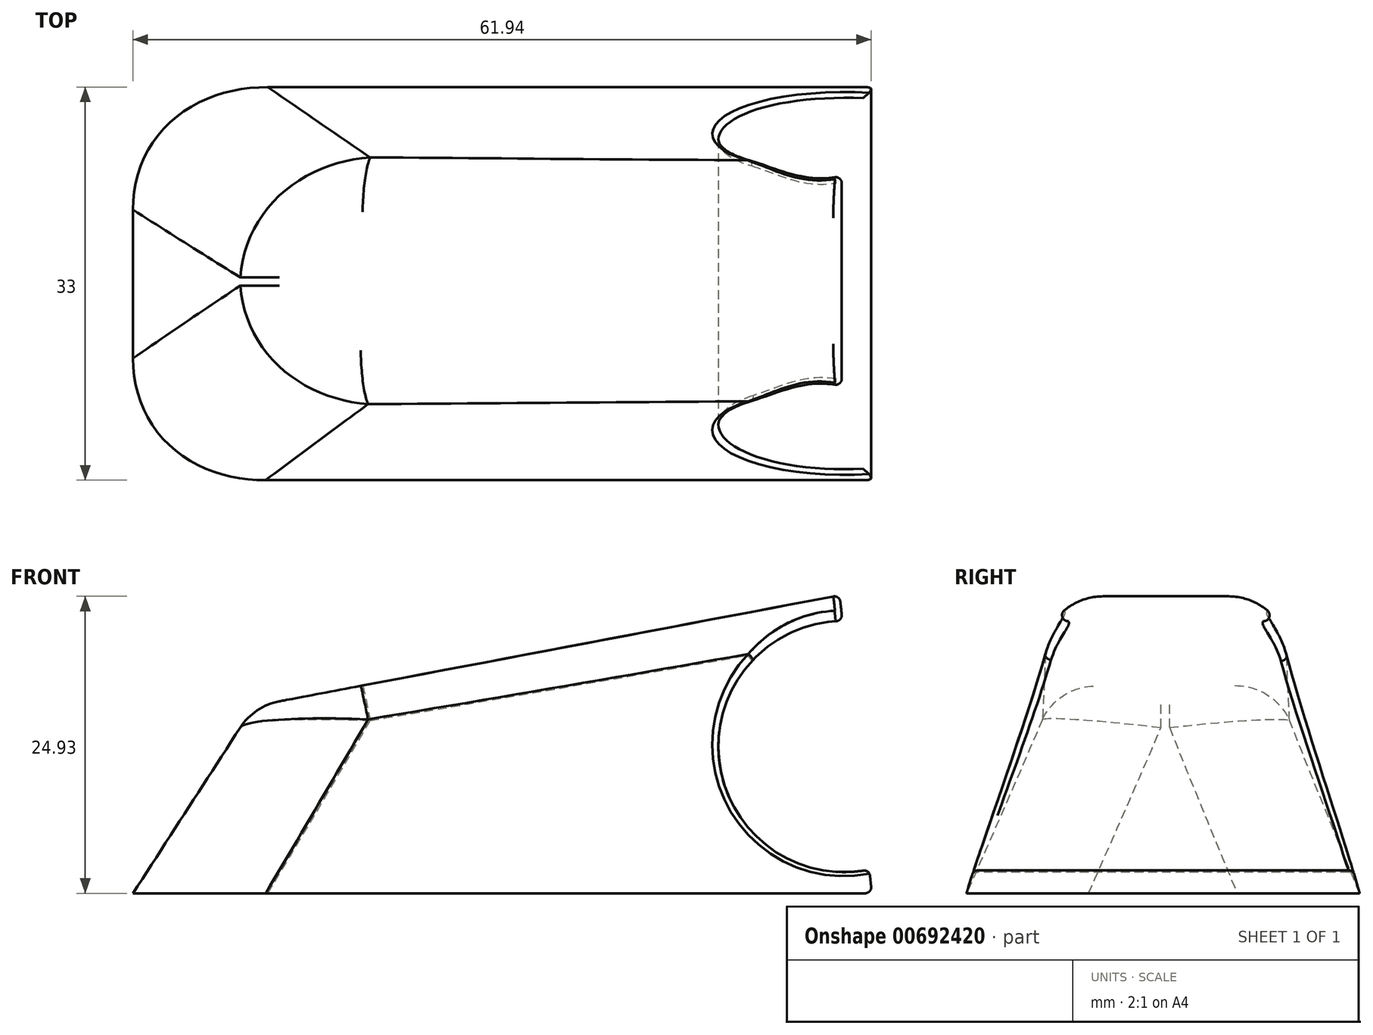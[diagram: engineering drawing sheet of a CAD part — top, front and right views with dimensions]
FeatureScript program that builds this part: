
annotation { "Feature Type Name" : "Feature", "Feature Type Description" : "" }
export const myFeature = defineFeature(function(context is Context, id is Id, definition is map)
    precondition{}
    {
        {
            var Q0;
            Q0=qCreatedBy(makeId("Top.planeOp"),FACE);
            var sketch = newSketch(context, id + "F0", { "sketchPlane" : qUnion([Q0])});
            skLineSegment(sketch, "E0.bottom", {"start": v(31, -16.5) * mm, "end": v(-31, -16.5) * mm});
            skLineSegment(sketch, "E0.top", {"start": v(31, 16.5) * mm, "end": v(-31, 16.5) * mm});
            skLineSegment(sketch, "E0.left", {"start": v(31, -16.5) * mm, "end": v(31, 16.5) * mm});
            skLineSegment(sketch, "E0.right", {"start": v(-31, -16.5) * mm, "end": v(-31, 16.5) * mm});
            skPoint(sketch, "E0.middle", {"position": v(0, 0) * mm});
            skSolve(sketch);
        }
        {
            var Q0;
            Q0=qCreatedBy(makeId("Front.planeOp"),FACE);
            var sketch = newSketch(context, id + "F1", { "sketchPlane" : qUnion([Q0])});
            skLineSegment(sketch, "E1", {"start": v(28.2, 25) * mm, "end": v(-24.6, 15) * mm});
            skSolve(sketch);
        }
        {
            var Q0;
            Q0 = qBodyType(qCreatedBy(id + "F1" ,EDGE), BodyType.WIRE);
            cPlane(context, id + "F2", {"entities" : qUnion([Q0]), "cplaneType" : CPlaneType.LINE_ANGLE, "offset" : 25 * mm, "angle" : 90 * degree, "width" : 150 * mm, "height" : 150 * mm});
        }
        {
            var Q0;
            Q0=qCreatedBy(id+"F2.planeOp",FACE);
            var sketch = newSketch(context, id + "F3", { "sketchPlane" : qUnion([Q0])});
            skLineSegment(sketch, "E2.bottom", {"start": v(-17.54, -8.74) * mm, "end": v(32.46, -8.74) * mm});
            skLineSegment(sketch, "E2.top", {"start": v(-17.54, 9.26) * mm, "end": v(32.46, 9.26) * mm});
            skLineSegment(sketch, "E2.left", {"start": v(-17.54, -8.74) * mm, "end": v(-17.54, 9.26) * mm});
            skLineSegment(sketch, "E2.right", {"start": v(32.46, -8.74) * mm, "end": v(32.46, 9.26) * mm});
            skSolve(sketch);
        }
        {
            var Q0;
            Q0 = qSketchRegion(id + "F3", true);
            var Q1;
            Q1=makeQuery(id+"F0.imprint","IMPRINT",FACE,{"disambiguationData":[TD([[makeQuery(id+"F0.imprint","IMPRINT",EDGE,{"derivedFrom":sQuery(id+"F0.wireOp",EDGE,"E0.bottom")}),-1.0]])]});
            loft(context, id + "F4", {"sheetProfilesArray" : [{ "sheetProfileEntities" : qUnion([Q0]) }, { "sheetProfileEntities" : qUnion([Q1]) }]});
        }
        {
            var Q0;
            Q0=qCreatedBy(makeId("Front.planeOp"),FACE);
            var sketch = newSketch(context, id + "F5", { "sketchPlane" : qUnion([Q0])});
            skCircle(sketch, "E3", {"center": v(28.67, 12.32) * mm, "radius": 10.54 * mm});
            skSolve(sketch);
        }
        {
            var Q0;
            Q0=makeQuery(id+"F5.imprint","IMPRINT",FACE,{"disambiguationData":[TD([[makeQuery(id+"F5.imprint","IMPRINT",EDGE,{"derivedFrom":sQuery(id+"F5.wireOp",EDGE,"E3")}),1.0]])]});
            extrude(context, id + "F6", {"entities" : qUnion([Q0]), "operationType" : NewBodyOperationType.REMOVE, "endBound" : BoundingType.SYMMETRIC, "oppositeDirection" : true, "depth" : 38.2 * mm, "offsetDistance" : 25 * mm});
        }
        {
            var Q0;
            Q0=makeQuery(id+"F4.opLoft","SWEPT_EDGE",EDGE,{"disambiguationData":[OSD([sQuery(id+"F0.wireOp",EDGE,"E0.bottom"),sQuery(id+"F0.wireOp",EDGE,"E0.right"),sQuery(id+"F3.wireOp",EDGE,"E2.bottom"),sQuery(id+"F3.wireOp",EDGE,"E2.left")])]});
            var Q1;
            Q1=makeQuery(id+"F4.opLoft","SWEPT_EDGE",EDGE,{"disambiguationData":[OSD([sQuery(id+"F0.wireOp",EDGE,"E0.top"),sQuery(id+"F0.wireOp",EDGE,"E0.right"),sQuery(id+"F3.wireOp",EDGE,"E2.top"),sQuery(id+"F3.wireOp",EDGE,"E2.left")])]});
            fillet(context, id + "F7", {"entities" : qUnion([Q0, Q1]), "radius" : 12 * mm, "tangentPropagation" : true, "allowEdgeOverflow" : false});
        }
        {
            var Q0;
            Q0=makeQuery(id+"F4.opLoft","MID_CAP_EDGE",EDGE,{"disambiguationData":[OSD([sQuery(id+"F3.wireOp",EDGE,"E2.bottom"),sQuery(id+"F3.wireOp",EDGE,"E2.left"),sQuery(id+"F3.wireOp",EDGE,"E2.right")])],"capPos":0.0});
            var Q1;
            Q1=makeQuery(id+"F4.opLoft","MID_CAP_EDGE",EDGE,{"disambiguationData":[OSD([sQuery(id+"F3.wireOp",EDGE,"E2.top"),sQuery(id+"F3.wireOp",EDGE,"E2.left"),sQuery(id+"F3.wireOp",EDGE,"E2.right")])],"capPos":0.0});
            fillet(context, id + "F8", {"entities" : qUnion([Q0, Q1]), "radius" : 5 * mm, "tangentPropagation" : true, "allowEdgeOverflow" : false});
        }
        {
            var Q0;
            Q0=makeQuery(id+"F6.boolean.opBoolean","INTERSECT",EDGE,{"disambiguationData":[OD(1.0)],"derivedFrom":[makeQuery(id+"F4.opLoft","SWEPT_FACE",FACE,{"disambiguationData":[OSD([sQuery(id+"F0.wireOp",EDGE,"E0.bottom"),sQuery(id+"F0.wireOp",EDGE,"E0.top"),sQuery(id+"F0.wireOp",EDGE,"E0.left"),sQuery(id+"F3.wireOp",EDGE,"E2.bottom"),sQuery(id+"F3.wireOp",EDGE,"E2.top"),sQuery(id+"F3.wireOp",EDGE,"E2.right")])]}),makeQuery(id+"F6.opExtrude","SWEPT_FACE",FACE,{"disambiguationData":[OSD([sQuery(id+"F5.wireOp",EDGE,"E3")])]})]});
            var Q1;
            Q1=makeQuery(id+"F6.boolean.opBoolean","INTERSECT",EDGE,{"disambiguationData":[OD(0.0)],"derivedFrom":[makeQuery(id+"F4.opLoft","SWEPT_FACE",FACE,{"disambiguationData":[OSD([sQuery(id+"F0.wireOp",EDGE,"E0.bottom"),sQuery(id+"F0.wireOp",EDGE,"E0.top"),sQuery(id+"F0.wireOp",EDGE,"E0.left"),sQuery(id+"F3.wireOp",EDGE,"E2.bottom"),sQuery(id+"F3.wireOp",EDGE,"E2.top"),sQuery(id+"F3.wireOp",EDGE,"E2.right")])]}),makeQuery(id+"F6.opExtrude","SWEPT_FACE",FACE,{"disambiguationData":[OSD([sQuery(id+"F5.wireOp",EDGE,"E3")])]})]});
            var Q2;
            Q2=makeQuery(id+"F4.opLoft","MID_CAP_EDGE",EDGE,{"disambiguationData":[OSD([sQuery(id+"F3.wireOp",EDGE,"E2.bottom"),sQuery(id+"F3.wireOp",EDGE,"E2.top"),sQuery(id+"F3.wireOp",EDGE,"E2.right")])],"capPos":0.0});
            var Q3;
            Q3=makeQuery(id+"F4.opLoft","MID_CAP_EDGE",EDGE,{"disambiguationData":[OSD([sQuery(id+"F0.wireOp",EDGE,"E0.bottom"),sQuery(id+"F0.wireOp",EDGE,"E0.top"),sQuery(id+"F0.wireOp",EDGE,"E0.left")])],"capPos":1.0});
            var Q4;
            Q4=makeQuery(id+"F6.boolean.opBoolean","INTERSECT",EDGE,{"derivedFrom":[makeQuery(id+"F4.opLoft","SWEPT_FACE",FACE,{"disambiguationData":[OSD([sQuery(id+"F0.wireOp",EDGE,"E0.bottom"),sQuery(id+"F0.wireOp",EDGE,"E0.left"),sQuery(id+"F0.wireOp",EDGE,"E0.right"),sQuery(id+"F3.wireOp",EDGE,"E2.bottom"),sQuery(id+"F3.wireOp",EDGE,"E2.left"),sQuery(id+"F3.wireOp",EDGE,"E2.right")])]}),makeQuery(id+"F6.opExtrude","SWEPT_FACE",FACE,{"disambiguationData":[OSD([sQuery(id+"F5.wireOp",EDGE,"E3")])]})]});
            var Q5;
            Q5=makeQuery(id+"F6.boolean.opBoolean","INTERSECT",EDGE,{"derivedFrom":[makeQuery(id+"F4.opLoft","SWEPT_FACE",FACE,{"disambiguationData":[OSD([sQuery(id+"F0.wireOp",EDGE,"E0.top"),sQuery(id+"F0.wireOp",EDGE,"E0.left"),sQuery(id+"F0.wireOp",EDGE,"E0.right"),sQuery(id+"F3.wireOp",EDGE,"E2.top"),sQuery(id+"F3.wireOp",EDGE,"E2.left"),sQuery(id+"F3.wireOp",EDGE,"E2.right")])]}),makeQuery(id+"F6.opExtrude","SWEPT_FACE",FACE,{"disambiguationData":[OSD([sQuery(id+"F5.wireOp",EDGE,"E3")])]})]});
            fillet(context, id + "F9", {"entities" : qUnion([Q0, Q1, Q2, Q3, Q4, Q5]), "radius" : 0.5 * mm, "tangentPropagation" : true, "allowEdgeOverflow" : false});
        }
    });
